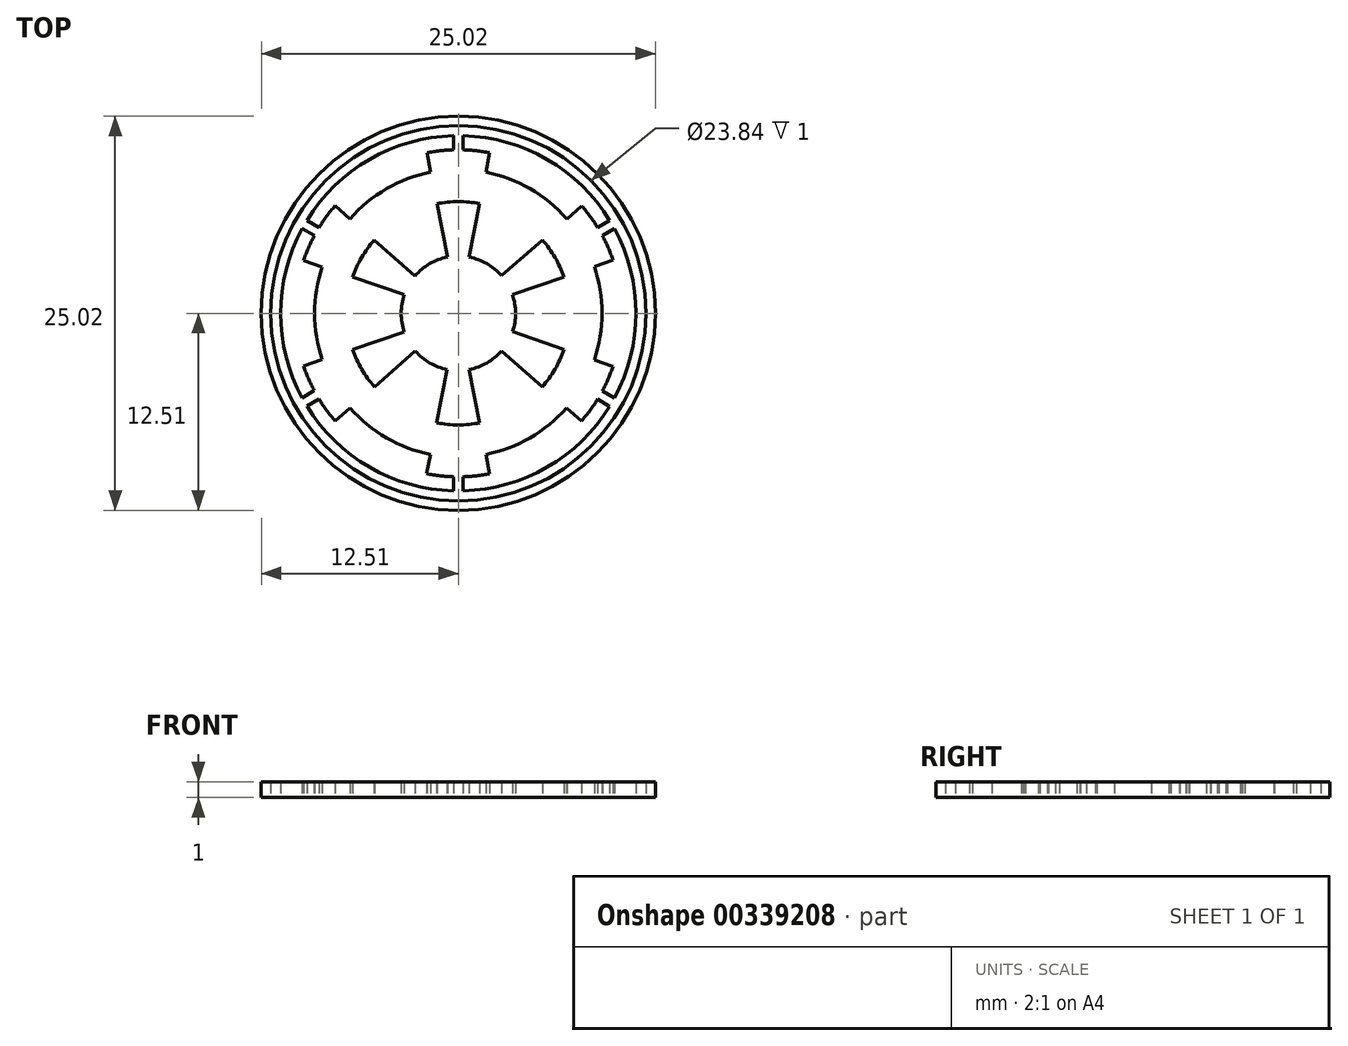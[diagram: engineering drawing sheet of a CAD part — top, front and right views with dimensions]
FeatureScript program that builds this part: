
annotation { "Feature Type Name" : "Feature", "Feature Type Description" : "" }
export const myFeature = defineFeature(function(context is Context, id is Id, definition is map)
    precondition{}
    {
        {
            var Q0;
            Q0=qCreatedBy(makeId("Top.planeOp"),FACE);
            var sketch = newSketch(context, id + "F0", { "sketchPlane" : qUnion([Q0])});
            skCircle(sketch, "E0", {"center": v(0, 0) * mm, "radius": 12.51 * mm});
            skPoint(sketch, "E0.centerSnap0", {"position": v(0, 12.5) * mm});
            skPoint(sketch, "E0.centerSnap1", {"position": v(-12.5, 0) * mm});
            skCircle(sketch, "E1", {"center": v(0, 0) * mm, "radius": 11.28 * mm});
            skCircle(sketch, "E2", {"center": v(0, 0) * mm, "radius": 3.63 * mm});
            skCircle(sketch, "E3", {"center": v(0, 0) * mm, "radius": 9.13 * mm});
            skCircle(sketch, "E4", {"center": v(0, 0) * mm, "radius": 10.39 * mm});
            skCircle(sketch, "E5", {"center": v(0, 0) * mm, "radius": 7.09 * mm});
            skCircle(sketch, "E6", {"center": v(0, 0) * mm, "radius": 11.92 * mm});
            skLineSegment(sketch, "E7", {"start": v(-0.7, 3.57) * mm, "end": v(-2, 10.2) * mm});
            skLineSegment(sketch, "E8", {"start": v(0.69, 3.57) * mm, "end": v(1.99, 10.2) * mm});
            skLineSegment(sketch, "E9", {"start": v(2.73, 2.4) * mm, "end": v(7.84, 6.82) * mm});
            skLineSegment(sketch, "E10", {"start": v(3.44, 1.18) * mm, "end": v(9.82, 3.38) * mm});
            skLineSegment(sketch, "E11", {"start": v(3.44, -1.17) * mm, "end": v(9.83, -3.37) * mm});
            skLineSegment(sketch, "E12", {"start": v(2.74, -2.4) * mm, "end": v(7.81, -6.85) * mm});
            skLineSegment(sketch, "E13", {"start": v(0.69, -3.57) * mm, "end": v(2, -10.2) * mm});
            skLineSegment(sketch, "E14", {"start": v(-0.7, -3.57) * mm, "end": v(-2.01, -10.2) * mm});
            skLineSegment(sketch, "E15", {"start": v(-2.73, -2.4) * mm, "end": v(-7.82, -6.84) * mm});
            skLineSegment(sketch, "E16", {"start": v(-3.44, -1.18) * mm, "end": v(-9.83, -3.35) * mm});
            skLineSegment(sketch, "E17", {"start": v(-3.44, 1.18) * mm, "end": v(-9.83, 3.35) * mm});
            skLineSegment(sketch, "E18", {"start": v(-2.75, 2.38) * mm, "end": v(-7.83, 6.83) * mm});
            skLineSegment(sketch, "E19", {"start": v(-0.3, -10.38) * mm, "end": v(-0.3, -11.28) * mm});
            skLineSegment(sketch, "E20", {"start": v(0.3, -10.38) * mm, "end": v(0.3, -11.28) * mm});
            skLineSegment(sketch, "E21", {"start": v(9.15, -4.92) * mm, "end": v(9.93, -5.37) * mm});
            skLineSegment(sketch, "E22", {"start": v(8.85, -5.44) * mm, "end": v(9.61, -5.91) * mm});
            skLineSegment(sketch, "E23", {"start": v(8.84, 5.46) * mm, "end": v(9.62, 5.9) * mm});
            skLineSegment(sketch, "E24", {"start": v(9.14, 4.93) * mm, "end": v(9.92, 5.37) * mm});
            skLineSegment(sketch, "E25", {"start": v(-0.3, 11.28) * mm, "end": v(-0.3, 10.38) * mm});
            skLineSegment(sketch, "E26", {"start": v(0.3, 11.28) * mm, "end": v(0.3, 10.38) * mm});
            skLineSegment(sketch, "E27", {"start": v(-9.62, 5.9) * mm, "end": v(-8.84, 5.45) * mm});
            skLineSegment(sketch, "E28", {"start": v(-9.93, 5.37) * mm, "end": v(-9.14, 4.94) * mm});
            skLineSegment(sketch, "E29", {"start": v(-9.92, -5.37) * mm, "end": v(-9.15, -4.92) * mm});
            skLineSegment(sketch, "E30", {"start": v(-9.62, -5.9) * mm, "end": v(-8.85, -5.45) * mm});
            skSolve(sketch);
        }
        {
            var Q0;
            Q0=makeQuery(id+"F0.imprint","IMPRINT",FACE,{"disambiguationData":[TD([[makeQuery(id+"F0.imprint","IMPRINT",EDGE,{"derivedFrom":sQuery(id+"F0.wireOp",EDGE,"E0")}),1.0]])]});
            var Q1;
            {var subQ4=sQuery(id+"F0.wireOp",EDGE,"E23");Q1=makeQuery(id+"F0.imprint","IMPRINT",FACE,{"disambiguationData":[TD([[makeQuery(id+"F0.imprint","IMPRINT",EDGE,{"derivedFrom":subQ4}),1.0]])]});}
            var Q2;
            {var subQ4=sQuery(id+"F0.wireOp",EDGE,"E21");Q2=makeQuery(id+"F0.imprint","IMPRINT",FACE,{"disambiguationData":[TD([[makeQuery(id+"F0.imprint","IMPRINT",EDGE,{"derivedFrom":subQ4}),1.0]])]});}
            var Q3;
            {var subQ4=sQuery(id+"F0.wireOp",EDGE,"E20");Q3=makeQuery(id+"F0.imprint","IMPRINT",FACE,{"disambiguationData":[TD([[makeQuery(id+"F0.imprint","IMPRINT",EDGE,{"derivedFrom":subQ4}),1.0]])]});}
            var Q4;
            {var subQ3=sQuery(id+"F0.wireOp",EDGE,"E19");Q4=makeQuery(id+"F0.imprint","IMPRINT",FACE,{"disambiguationData":[TD([[makeQuery(id+"F0.imprint","IMPRINT",EDGE,{"derivedFrom":subQ3}),-1.0]])]});}
            var Q5;
            {var subQ4=sQuery(id+"F0.wireOp",EDGE,"E28");Q5=makeQuery(id+"F0.imprint","IMPRINT",FACE,{"disambiguationData":[TD([[makeQuery(id+"F0.imprint","IMPRINT",EDGE,{"derivedFrom":subQ4}),-1.0]])]});}
            var Q6;
            {var subQ4=sQuery(id+"F0.wireOp",EDGE,"E25");Q6=makeQuery(id+"F0.imprint","IMPRINT",FACE,{"disambiguationData":[TD([[makeQuery(id+"F0.imprint","IMPRINT",EDGE,{"derivedFrom":subQ4}),-1.0]])]});}
            var Q7;
            {var subQ0=sQuery(id+"F0.wireOp",EDGE,"E7");var subQ1=sQuery(id+"F0.wireOp",EDGE,"E3");var subQ2=makeQuery(id+"F0.imprint","INTERSECT",VERTEX,{"derivedFrom":[subQ1,subQ0]});Q7=makeQuery(id+"F0.imprint","IMPRINT",FACE,{"disambiguationData":[TD([[makeQuery(id+"F0.imprint","IMPRINT",EDGE,{"disambiguationData":[TD([[subQ2,-1.0]])],"derivedFrom":subQ1}),-1.0]])]});}
            var Q8;
            {var subQ0=sQuery(id+"F0.wireOp",EDGE,"E17");var subQ1=sQuery(id+"F0.wireOp",EDGE,"E3");var subQ2=makeQuery(id+"F0.imprint","INTERSECT",VERTEX,{"derivedFrom":[subQ1,subQ0]});Q8=makeQuery(id+"F0.imprint","IMPRINT",FACE,{"disambiguationData":[TD([[makeQuery(id+"F0.imprint","IMPRINT",EDGE,{"disambiguationData":[TD([[subQ2,-1.0]])],"derivedFrom":subQ1}),-1.0]])]});}
            var Q9;
            {var subQ0=sQuery(id+"F0.wireOp",EDGE,"E15");var subQ1=sQuery(id+"F0.wireOp",EDGE,"E3");var subQ2=makeQuery(id+"F0.imprint","INTERSECT",VERTEX,{"derivedFrom":[subQ1,subQ0]});Q9=makeQuery(id+"F0.imprint","IMPRINT",FACE,{"disambiguationData":[TD([[makeQuery(id+"F0.imprint","IMPRINT",EDGE,{"disambiguationData":[TD([[subQ2,-1.0]])],"derivedFrom":subQ1}),-1.0]])]});}
            var Q10;
            {var subQ0=sQuery(id+"F0.wireOp",EDGE,"E13");var subQ1=sQuery(id+"F0.wireOp",EDGE,"E3");var subQ2=makeQuery(id+"F0.imprint","INTERSECT",VERTEX,{"derivedFrom":[subQ1,subQ0]});Q10=makeQuery(id+"F0.imprint","IMPRINT",FACE,{"disambiguationData":[TD([[makeQuery(id+"F0.imprint","IMPRINT",EDGE,{"disambiguationData":[TD([[subQ2,-1.0]])],"derivedFrom":subQ1}),-1.0]])]});}
            var Q11;
            {var subQ0=sQuery(id+"F0.wireOp",EDGE,"E10");var subQ1=sQuery(id+"F0.wireOp",EDGE,"E3");var subQ2=makeQuery(id+"F0.imprint","INTERSECT",VERTEX,{"derivedFrom":[subQ1,subQ0]});Q11=makeQuery(id+"F0.imprint","IMPRINT",FACE,{"disambiguationData":[TD([[makeQuery(id+"F0.imprint","IMPRINT",EDGE,{"disambiguationData":[TD([[subQ2,1.0]])],"derivedFrom":subQ1}),-1.0]])]});}
            var Q12;
            {var subQ0=sQuery(id+"F0.wireOp",EDGE,"E9");var subQ1=sQuery(id+"F0.wireOp",EDGE,"E3");var subQ2=makeQuery(id+"F0.imprint","INTERSECT",VERTEX,{"derivedFrom":[subQ1,subQ0]});Q12=makeQuery(id+"F0.imprint","IMPRINT",FACE,{"disambiguationData":[TD([[makeQuery(id+"F0.imprint","IMPRINT",EDGE,{"disambiguationData":[TD([[subQ2,-1.0]])],"derivedFrom":subQ1}),-1.0]])]});}
            var Q13;
            {var subQ0=sQuery(id+"F0.wireOp",EDGE,"E2");var subQ8=makeQuery(id+"F0.imprint","INTERSECT",VERTEX,{"derivedFrom":[subQ0,sQuery(id+"F0.wireOp",EDGE,"E9")]});Q13=makeQuery(id+"F0.imprint","IMPRINT",FACE,{"disambiguationData":[TD([[makeQuery(id+"F0.imprint","IMPRINT",EDGE,{"disambiguationData":[TD([[subQ8,1.0]])],"derivedFrom":subQ0}),1.0]])]});}
            var Q14;
            {var subQ0=sQuery(id+"F0.wireOp",EDGE,"E7");var subQ1=sQuery(id+"F0.wireOp",EDGE,"E2");var subQ2=makeQuery(id+"F0.imprint","INTERSECT",VERTEX,{"derivedFrom":[subQ1,subQ0]});Q14=makeQuery(id+"F0.imprint","IMPRINT",FACE,{"disambiguationData":[TD([[makeQuery(id+"F0.imprint","IMPRINT",EDGE,{"disambiguationData":[TD([[subQ2,1.0]])],"derivedFrom":subQ1}),-1.0]])]});}
            var Q15;
            {var subQ0=sQuery(id+"F0.wireOp",EDGE,"E17");var subQ1=sQuery(id+"F0.wireOp",EDGE,"E2");var subQ2=makeQuery(id+"F0.imprint","INTERSECT",VERTEX,{"derivedFrom":[subQ1,subQ0]});Q15=makeQuery(id+"F0.imprint","IMPRINT",FACE,{"disambiguationData":[TD([[makeQuery(id+"F0.imprint","IMPRINT",EDGE,{"disambiguationData":[TD([[subQ2,1.0]])],"derivedFrom":subQ1}),-1.0]])]});}
            var Q16;
            {var subQ0=sQuery(id+"F0.wireOp",EDGE,"E15");var subQ1=sQuery(id+"F0.wireOp",EDGE,"E2");var subQ2=makeQuery(id+"F0.imprint","INTERSECT",VERTEX,{"derivedFrom":[subQ1,subQ0]});Q16=makeQuery(id+"F0.imprint","IMPRINT",FACE,{"disambiguationData":[TD([[makeQuery(id+"F0.imprint","IMPRINT",EDGE,{"disambiguationData":[TD([[subQ2,1.0]])],"derivedFrom":subQ1}),-1.0]])]});}
            var Q17;
            {var subQ0=sQuery(id+"F0.wireOp",EDGE,"E13");var subQ1=sQuery(id+"F0.wireOp",EDGE,"E2");var subQ2=makeQuery(id+"F0.imprint","INTERSECT",VERTEX,{"derivedFrom":[subQ1,subQ0]});Q17=makeQuery(id+"F0.imprint","IMPRINT",FACE,{"disambiguationData":[TD([[makeQuery(id+"F0.imprint","IMPRINT",EDGE,{"disambiguationData":[TD([[subQ2,1.0]])],"derivedFrom":subQ1}),-1.0]])]});}
            var Q18;
            {var subQ0=sQuery(id+"F0.wireOp",EDGE,"E11");var subQ1=sQuery(id+"F0.wireOp",EDGE,"E2");var subQ2=makeQuery(id+"F0.imprint","INTERSECT",VERTEX,{"derivedFrom":[subQ1,subQ0]});Q18=makeQuery(id+"F0.imprint","IMPRINT",FACE,{"disambiguationData":[TD([[makeQuery(id+"F0.imprint","IMPRINT",EDGE,{"disambiguationData":[TD([[subQ2,1.0]])],"derivedFrom":subQ1}),-1.0]])]});}
            var Q19;
            {var subQ0=sQuery(id+"F0.wireOp",EDGE,"E9");var subQ1=sQuery(id+"F0.wireOp",EDGE,"E2");var subQ2=makeQuery(id+"F0.imprint","INTERSECT",VERTEX,{"derivedFrom":[subQ1,subQ0]});Q19=makeQuery(id+"F0.imprint","IMPRINT",FACE,{"disambiguationData":[TD([[makeQuery(id+"F0.imprint","IMPRINT",EDGE,{"disambiguationData":[TD([[subQ2,1.0]])],"derivedFrom":subQ1}),-1.0]])]});}
            extrude(context, id + "F1", {"entities" : qUnion([Q0, Q1, Q2, Q3, Q4, Q5, Q6, Q7, Q8, Q9, Q10, Q11, Q12, Q13, Q14, Q15, Q16, Q17, Q18, Q19]), "flatOperationType" : FlatOperationType.REMOVE, "thickness1" : 5 * mm, "thickness2" : 0 * mm, "thickness" : 5 * mm, "offsetDistance" : 25 * mm, "startOffsetBound" : StartOffsetType.BLIND, "startOffsetDistance" : 25 * mm, "depth" : 1 * mm, "domain" : OperationDomain.MODEL});
        }
    });
